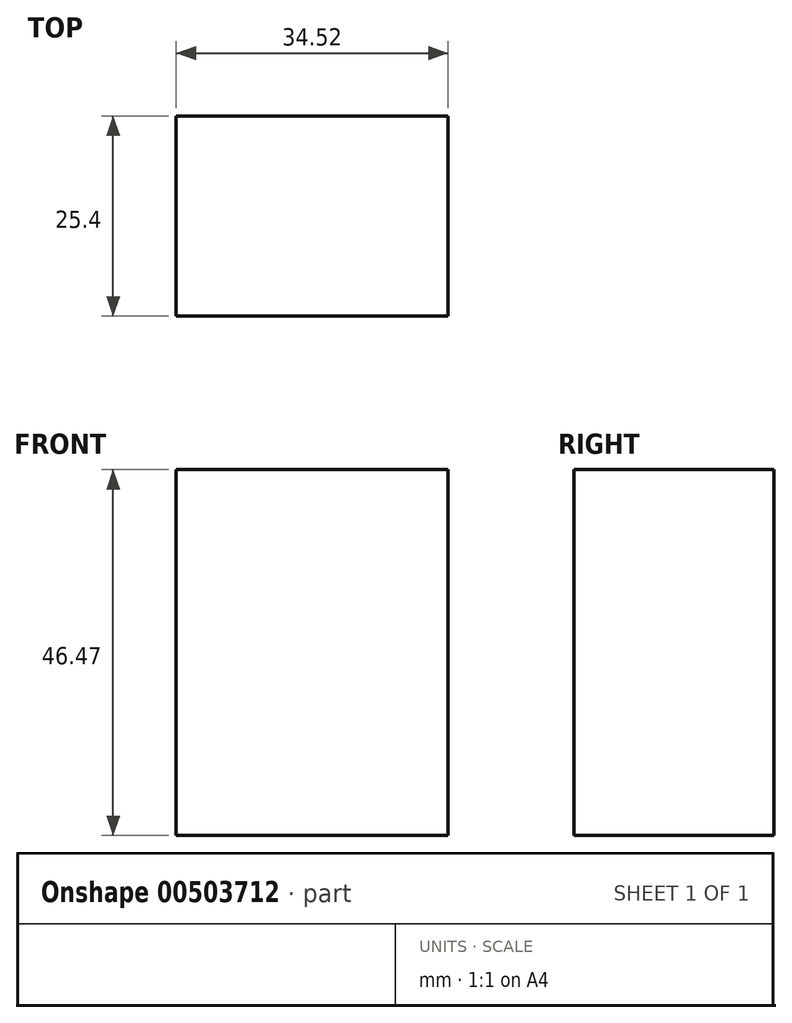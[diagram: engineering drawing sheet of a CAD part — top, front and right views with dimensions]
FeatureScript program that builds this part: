
annotation { "Feature Type Name" : "Feature", "Feature Type Description" : "" }
export const myFeature = defineFeature(function(context is Context, id is Id, definition is map)
    precondition{}
    {
        {
            var Q0;
            Q0=qCreatedBy(makeId("Front.planeOp"),FACE);
            var sketch = newSketch(context, id + "F0", { "sketchPlane" : qUnion([Q0])});
            skLineSegment(sketch, "E0.bottom", {"start": v(0, 0) * mm, "end": v(-34.52, 0) * mm});
            skLineSegment(sketch, "E0.top", {"start": v(0, 46.47) * mm, "end": v(-34.52, 46.47) * mm});
            skLineSegment(sketch, "E0.left", {"start": v(0, 0) * mm, "end": v(0, 46.47) * mm});
            skLineSegment(sketch, "E0.right", {"start": v(-34.52, 0) * mm, "end": v(-34.52, 46.47) * mm});
            skSolve(sketch);
        }
        {
            var Q0;
            Q0 = qSketchRegion(id + "Fq6O2GRYfJ3pXFh_0", true);
            var Q1;
            Q1=makeQuery(id+"F0.imprint","IMPRINT",FACE,{"disambiguationData":[TD([[makeQuery(id+"F0.imprint","IMPRINT",EDGE,{"derivedFrom":sQuery(id+"F0.wireOp",EDGE,"E0.bottom")}),-1.0]])]});
            extrude(context, id + "F1", {"entities" : qUnion([Q0, Q1]), "depth" : 25.4 * mm});
        }
    });
